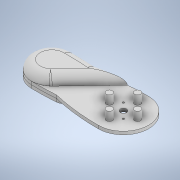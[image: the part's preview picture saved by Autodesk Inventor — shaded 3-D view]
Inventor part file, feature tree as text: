
AUTODESK INVENTOR PART (.ipt)
format: ipt  version: 2020.3 (Build 243373000, 373)  size: 431,616 bytes
history: native  units: mm
features: sketch x9, extrude x8, fillet x3, hole x1
ambient origin geometry x8: Origin, YZ Plane, XZ Plane, XY Plane, X Axis, Y Axis, Z Axis, Center Point
bodies: Body1 (feature_tree)
feature tree (21):
  extrude  "Extrusion2"  Depth=140.0mm
  extrude  "Extrusion3"  Depth=70.0mm
  extrude  "Extrusion4"  Depth=10.0mm
  hole  "Hole1"  [1 undecoded]
  extrude  "Extrusion5"  Depth=45.0mm
  extrude  "Extrusion6"  Depth=9.8mm
  fillet  "Fillet1"  Radius=14.0mm
  extrude  "Extrusion7"  Depth=10.0mm TaperAngle=0.0deg
  extrude  "Extrusion8"  Depth=13.89mm TaperAngle=0.0deg
  extrude  "Extrusion11"  Depth=13.89mm TaperAngle=0.0deg
  fillet  "Fillet6"  Radius=12.0mm
  fillet  "Fillet7"  Radius=16.0mm
  sketch  "Sketch1"  dims[d23=5.0mm d24=0.0mm d25=140.0mm]
  sketch  "Sketch2"  dims[d26=30.0mm d27=70.0mm]
  sketch  "Sketch3"  dims[d28=30.0mm d29=10.0mm]
  sketch  "Sketch4"  dims[d30=50.0mm d31=45.0mm]
  sketch  "Sketch5"  dims[d32=45.0mm d33=45.0mm]
  sketch  "Sketch6"  dims[d34=45.0mm]
  sketch  "Sketch7"  dims[d35=10.0mm d36=45.0mm d37=9.8mm d38=9.8mm d39=9.8mm d40=1.0mm d41=2.0mm d42=2.0mm d43=2.0mm d44=2.0mm d45=2.0mm d47=9.8mm d48=14.0mm d49=0.0mm]
  sketch  "Sketch8"  dims[d50=10.0mm d51=45.0mm d52=9.8mm d53=9.8mm d54=9.8mm d55=1.0mm d56=2.0mm d57=2.0mm d58=2.0mm d59=2.0mm d60=2.0mm d61=9.8mm d62=10.0mm d63=0.0mm]
  sketch  "Sketch10"  dims[d65=40.0mm d66=20.0mm d67=360.0deg d68=3.0mm d69=3.0mm d70=3.0mm d71=3.0mm d72=3.0mm d73=6.0mm d74=5.6mm d75=3.2mm d76=90.0deg d77=8.0mm d78=20.594885mm d79=5.0mm d80=0.0mm d81=5.0mm d82=0.0mm d83=12.0mm d84=16.0mm d85=5.0mm d86=0.0mm d87=11.0mm d88=2.0mm d89=0.0mm d102=140.0mm d103=30.0mm d104=70.0mm d105=30.0mm d106=10.0mm d107=50.0mm d108=45.0mm d109=45.0mm d110=45.0mm d111=45.0mm d112=90.0mm d120=14.0mm d121=0.0mm d127=100.0mm d128=65.0mm d129=140.0mm d130=30.0mm d131=70.0mm d132=30.0mm d133=10.0mm d134=50.0mm d135=45.0mm d136=45.0mm d137=45.0mm d138=45.0mm d139=13.999mm d140=13.89mm]
note: 1 required parameter value undecoded (feature->parameter linkage not recoverable at this tier; creation-order binding heuristic only, values carry confidence <= 0.55)
